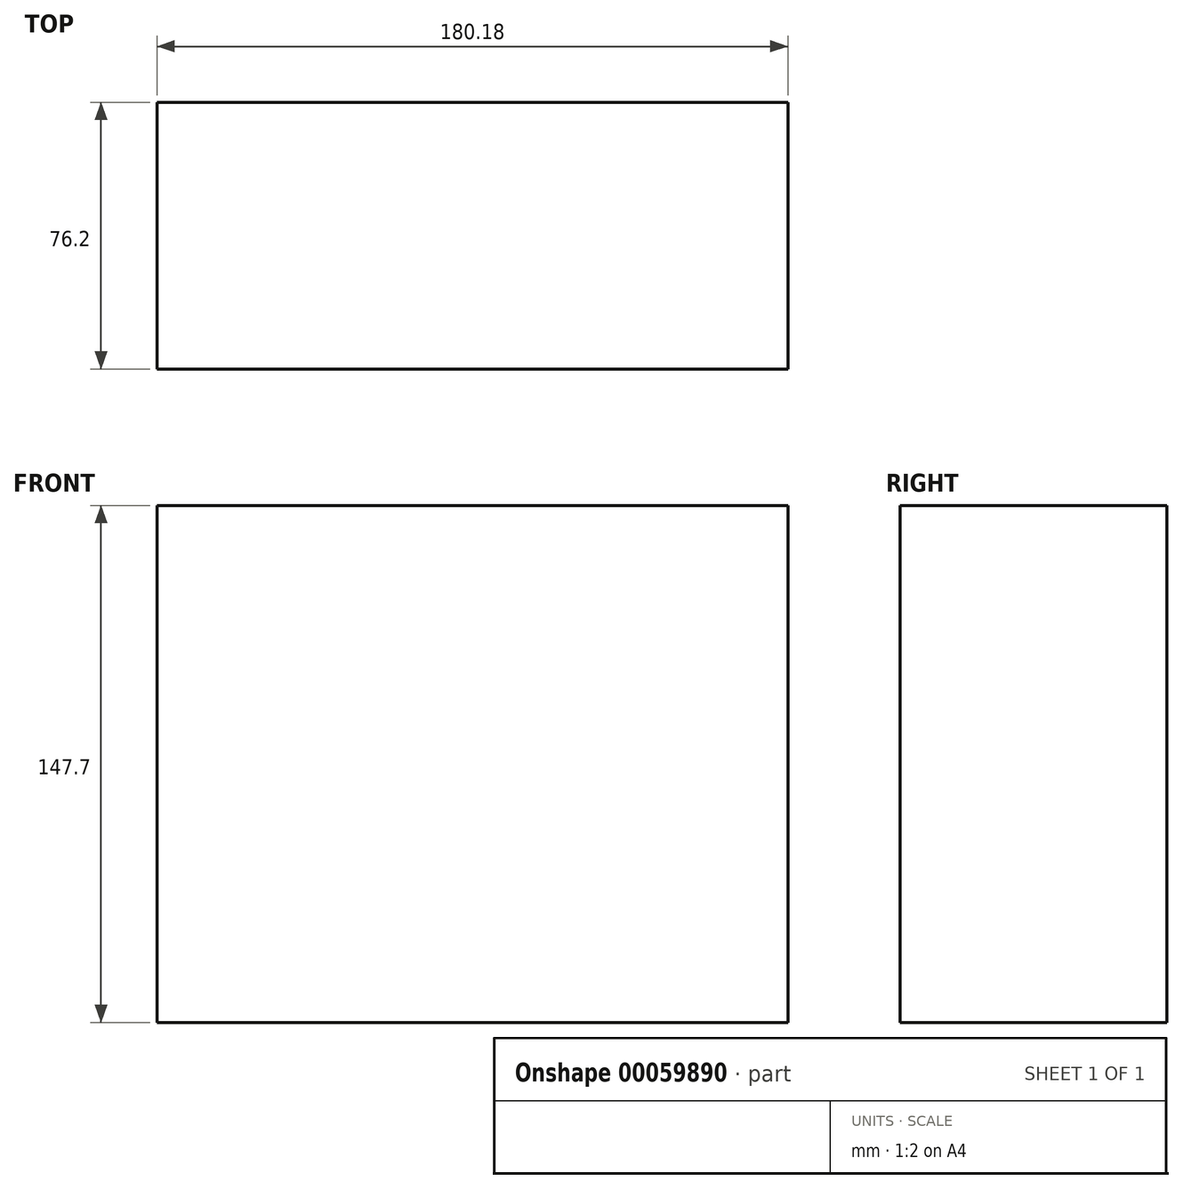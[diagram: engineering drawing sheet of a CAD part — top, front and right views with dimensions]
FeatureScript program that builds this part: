
annotation { "Feature Type Name" : "Feature", "Feature Type Description" : "" }
export const myFeature = defineFeature(function(context is Context, id is Id, definition is map)
    precondition{}
    {
        {
            var Q0;
            Q0=qCreatedBy(makeId("Front.planeOp"),FACE);
            var sketch = newSketch(context, id + "F0", { "sketchPlane" : qUnion([Q0])});
            skLineSegment(sketch, "E0.rect.bottom", {"start": v(75.2, 65.8) * mm, "end": v(-104.99, 65.8) * mm});
            skLineSegment(sketch, "E0.rect.top", {"start": v(75.2, -81.9) * mm, "end": v(-104.99, -81.9) * mm});
            skLineSegment(sketch, "E0.rect.left", {"start": v(75.2, 65.8) * mm, "end": v(75.2, -81.9) * mm});
            skLineSegment(sketch, "E0.rect.right", {"start": v(-104.99, 65.8) * mm, "end": v(-104.99, -81.9) * mm});
            skPoint(sketch, "E0.rect.middle", {"position": v(-14.9, -8.06) * mm});
            skSolve(sketch);
        }
        {
            var Q0;
            Q0 = qSketchRegion(id + "F0", true);
            extrude(context, id + "F1", {"entities" : qUnion([Q0]), "depth" : 76.2 * mm});
        }
    });
